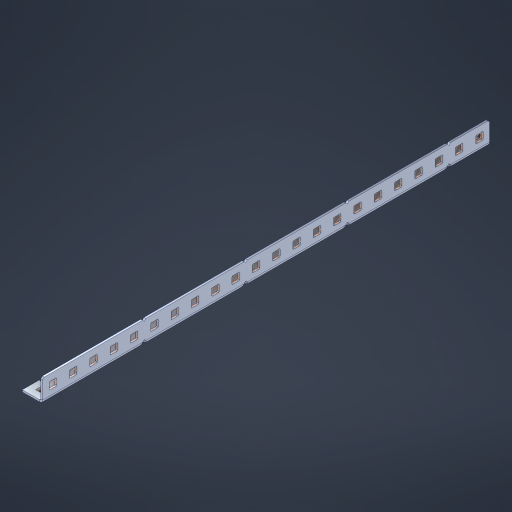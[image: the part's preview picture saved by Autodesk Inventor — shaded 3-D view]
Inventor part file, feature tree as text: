
AUTODESK INVENTOR PART (.ipt)
format: ipt  version: 2023 (Build 270158000, 158)  size: 1,003,008 bytes
history: native  units: in
note: dims shown in document units (in); Inventor stores cm internally (conversion verified against a paired STEP export)
features: other x73, extrude x64, sheet_metal_op x11, sketch x10, pattern_linear x2, mirror x1, chamfer x1
ambient origin geometry x8: Origin, YZ Plane, XZ Plane, XY Plane, X Axis, Y Axis, Z Axis, Center Point
bodies: Solid1 (feature_tree), Body (feature_tree)
feature tree (162):
  sheet_metal_op  "Flanges"
  other  "Flange Pattern Plane"
  other  "Flange Pattern Sketch"
  sheet_metal_op  "Flange Pattern"
  sheet_metal_op  "Body Pattern"
  pattern_linear  "Center Pattern"  Spacing1=0.0469in  [1 undecoded]
  other  "Arc Length"
  mirror  "Notch Mirror"
  pattern_linear  "Notch Pattern"  Spacing1=0.182in  [1 undecoded]
  chamfer  "End Chamfer"
  extrude  "Half Cut"  Depth=0.02in
  sketch  "Sketch1"  dims[d0=1.0in]
  other  "Plate1"
  sketch  "Sketch2"  dims[d1=11.0in]
  other  "Plate2"
  sheet_metal_op  "Bend1"
  sheet_metal_op  "Corner1"
  sketch  "Sketch3"  dims[d2=0.0469in]
  sketch  "Sketch7"  dims[d3=0.0469in]
  other  "Srf1"
  other  "Srf2"
  sketch  "Sketch8"  dims[d4=0.0234in]
  sketch  "Sketch9"  dims[d5=0.0938in]
  other  "Srf91"
  sheet_metal_op  "Body Pattern Sketch"
  other  "Srf92"
  sketch  "Sketch13"  dims[d6=0.0469in]
  sketch  "Sketch14"  dims[d7=0.5in d8=90.0deg d9=0.0312in]
  sketch  "Sketch15"  dims[d10=0.1875in]
  sketch  "Sketch16"  dims[d11=0.0469in d12=0.0469in d16=0.182in d17=0.02in d18=0.0469in d19=0.0in d20=0.25in d21=0.25in d38=8.6614in d40=0.5in d41=0.3937in d43=1.0in d46=0.172in d47=1.0in d48=0.0in d49=0.182in d50=0.02in d51=0.25in d52=0.25in d53=0.0469in d54=0.0in d55=0.172in d56=1.0in d57=0.0in d58=0.25in d60=8.6614in d62=0.5in d63=0.3937in d65=0.5in d85=0.1227in d86=0.1659in d88=0.04in d89=0.0469in d90=0.0in d91=0.04in d92=0.0491in d95=2.5in d96=0.04in d97=0.25in d98=45.0deg d99=0.25in d100=0.5in d101=0.0in d102=2.497in d106=0.182in d107=0.02in d108=0.5in d109=0.5in d110=0.0469in d111=0.0in d112=0.172in d113=0.5in d114=0.0in d117=0.5in d118=0.5in d119=0.5in]
  other  "Srf786"
  other  "Srf823"
  other  "Srf824"
  other  "Srf825"
  other  "Srf826"
  other  "Srf827"
  other  "Srf828"
  other  "Srf829"
  other  "Srf856"
  other  "Srf857"
  other  "Srf858"
  other  "Srf859"
  other  "Srf860"
  other  "Srf861"
  other  "Srf862"
  other  "Srf889"
  other  "Srf890"
  other  "Srf891"
  other  "Srf892"
  other  "Srf893"
  other  "Srf894"
  other  "Srf895"
  other  "Srf896"
  other  "Srf922"
  other  "Srf923"
  other  "Srf924"
  other  "Srf925"
  other  "Srf926"
  other  "Srf959"
  other  "Srf960"
  other  "Srf961"
  other  "Srf962"
  other  "Srf963"
  other  "Srf996"
  other  "Srf997"
  other  "Srf998"
  other  "Srf999"
  other  "Srf1000"
  other  "Srf1143"
  other  "Srf1144"
  other  "Srf1145"
  other  "Srf1146"
  other  "Srf1147"
  other  "Srf1148"
  other  "Srf1149"
  other  "Srf1150"
  other  "Srf1199"
  other  "Srf1200"
  other  "Srf1201"
  other  "Srf1202"
  other  "Srf1203"
  other  "Srf1204"
  other  "Srf1205"
  other  "Srf1206"
  other  "Srf1255"
  other  "Srf1256"
  other  "Srf1257"
  other  "Srf1258"
  other  "Srf1259"
  other  "Srf1260"
  other  "Srf1261"
  other  "Srf1262"
  sheet_metal_op  "Flange Stamp"
  sheet_metal_op  "Flange Circle"
  sheet_metal_op  "Body Stamp"
  sheet_metal_op  "Body Circle"
  other  "Center Stamp"
  other  "Center Circle"
  sheet_metal_op  "Notch"
  extrude  "ExtrusionSrf2"  Depth=0.0469in
  extrude  "ExtrusionSrf92"  TaperAngle=0.0deg  [1 undecoded]
  extrude  "ExtrusionSrf823"  Depth=0.25in
  extrude  "ExtrusionSrf824"  Depth=0.25in
  extrude  "ExtrusionSrf825"  Depth=0.5in
  extrude  "ExtrusionSrf826"  Depth=0.5in
  extrude  "ExtrusionSrf827"  Depth=1.0in TaperAngle=0.0deg
  extrude  "ExtrusionSrf828"  Depth=0.182in
  extrude  "ExtrusionSrf829"  Depth=0.02in
  extrude  "ExtrusionSrf856"  Depth=0.25in
  extrude  "ExtrusionSrf857"  Depth=0.25in
  extrude  "ExtrusionSrf858"  Depth=0.0469in
  extrude  "ExtrusionSrf859"  TaperAngle=0.0deg  [1 undecoded]
  extrude  "ExtrusionSrf860"  Depth=0.5in
  extrude  "ExtrusionSrf861"  Depth=1.0in TaperAngle=0.0deg
  extrude  "ExtrusionSrf862"  Depth=0.25in
  extrude  "ExtrusionSrf889"  Depth=0.5in
  extrude  "ExtrusionSrf890"  Depth=0.5in
  extrude  "ExtrusionSrf891"  Depth=0.5in
  extrude  "ExtrusionSrf892"  Depth=0.5in
  extrude  "ExtrusionSrf893"  Depth=0.5in
  extrude  "ExtrusionSrf894"  Depth=0.0469in
  extrude  "ExtrusionSrf895"  TaperAngle=0.0deg  [1 undecoded]
  extrude  "ExtrusionSrf896"  Depth=0.5in
  extrude  "ExtrusionSrf922"  Depth=0.5in
  extrude  "ExtrusionSrf923"  Depth=2.5in
  extrude  "ExtrusionSrf924"  Depth=0.25in TaperAngle=45.0deg
  extrude  "ExtrusionSrf925"  Depth=0.25in
  extrude  "ExtrusionSrf926"  Depth=0.5in TaperAngle=0.0deg
  extrude  "ExtrusionSrf959"  Depth=0.5in
  extrude  "ExtrusionSrf960"  Depth=0.182in
  extrude  "ExtrusionSrf961"  Depth=0.02in
  extrude  "ExtrusionSrf962"  Depth=0.5in
  extrude  "ExtrusionSrf963"  Depth=0.5in
  extrude  "ExtrusionSrf996"  Depth=0.0469in
  extrude  "ExtrusionSrf997"  TaperAngle=0.0deg  [1 undecoded]
  extrude  "ExtrusionSrf998"  Depth=0.5in
  extrude  "ExtrusionSrf999"  Depth=0.5in TaperAngle=0.0deg
  extrude  "ExtrusionSrf1000"  Depth=0.5in
  extrude  "ExtrusionSrf1143"  Depth=0.5in
  extrude  "ExtrusionSrf1144"  Depth=0.5in
  extrude  "ExtrusionSrf1145"  [1 undecoded]
  extrude  "ExtrusionSrf1146"  [1 undecoded]
  extrude  "ExtrusionSrf1147"  [1 undecoded]
  extrude  "ExtrusionSrf1148"  [1 undecoded]
  extrude  "ExtrusionSrf1149"  [1 undecoded]
  extrude  "ExtrusionSrf1150"  [1 undecoded]
  extrude  "ExtrusionSrf1199"  [1 undecoded]
  extrude  "ExtrusionSrf1200"  [1 undecoded]
  extrude  "ExtrusionSrf1201"  [1 undecoded]
  extrude  "ExtrusionSrf1202"  [1 undecoded]
  extrude  "ExtrusionSrf1203"  [1 undecoded]
  extrude  "ExtrusionSrf1204"  [1 undecoded]
  extrude  "ExtrusionSrf1205"  [1 undecoded]
  extrude  "ExtrusionSrf1206"  [1 undecoded]
  extrude  "ExtrusionSrf1255"  [1 undecoded]
  extrude  "ExtrusionSrf1256"  [1 undecoded]
  extrude  "ExtrusionSrf1257"  [1 undecoded]
  extrude  "ExtrusionSrf1258"  [1 undecoded]
  extrude  "ExtrusionSrf1259"  [1 undecoded]
  extrude  "ExtrusionSrf1260"  [1 undecoded]
  extrude  "ExtrusionSrf1261"  [1 undecoded]
  extrude  "ExtrusionSrf1262"  [1 undecoded]
note: 28 required parameter values undecoded (feature->parameter linkage not recoverable at this tier; creation-order binding heuristic only, values carry confidence <= 0.55)
